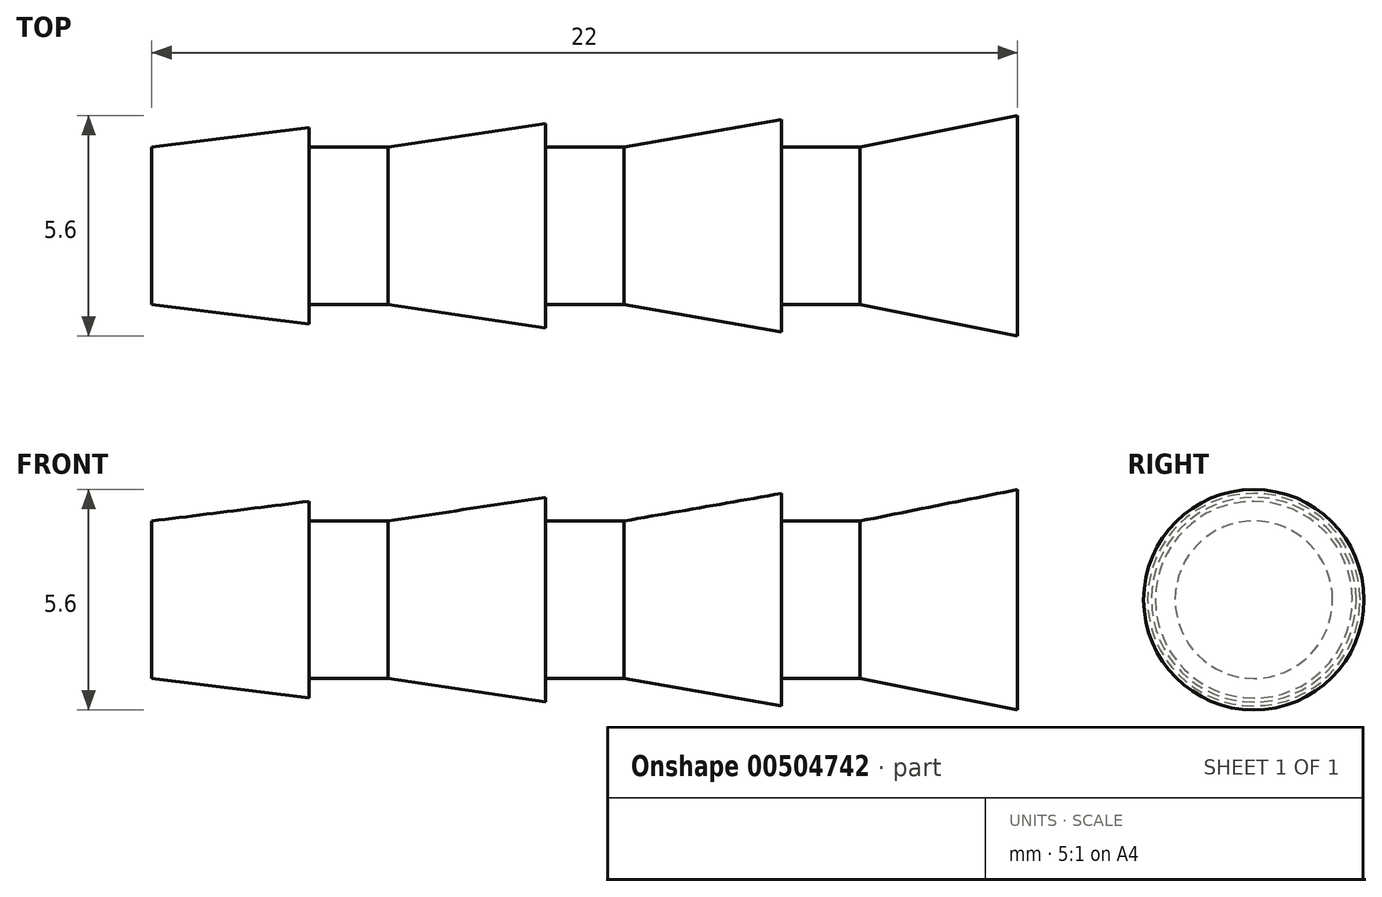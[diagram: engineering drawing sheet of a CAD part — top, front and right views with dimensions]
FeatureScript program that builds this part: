
annotation { "Feature Type Name" : "Feature", "Feature Type Description" : "" }
export const myFeature = defineFeature(function(context is Context, id is Id, definition is map)
    precondition{}
    {
        {
            var Q0;
            Q0=qCreatedBy(makeId("Front.planeOp"),FACE);
            var sketch = newSketch(context, id + "F0", { "sketchPlane" : qUnion([Q0])});
            skLineSegment(sketch, "E0", {"start": v(-13.38, 0) * mm, "end": v(33.35, 0) * mm, "construction": true});
            skLineSegment(sketch, "E1", {"start": v(-10.78, 0) * mm, "end": v(-10.78, 2) * mm});
            skLineSegment(sketch, "E2", {"start": v(-10.78, 2) * mm, "end": v(-6.78, 2.5) * mm});
            skLineSegment(sketch, "E3", {"start": v(-6.78, 2.5) * mm, "end": v(-6.78, 2) * mm});
            skLineSegment(sketch, "E4", {"start": v(-6.78, 2) * mm, "end": v(-4.78, 2) * mm});
            skLineSegment(sketch, "E5", {"start": v(-4.78, 2) * mm, "end": v(-0.78, 2.6) * mm});
            skLineSegment(sketch, "E6", {"start": v(-0.78, 2.6) * mm, "end": v(-0.78, 2) * mm});
            skLineSegment(sketch, "E7", {"start": v(-0.78, 2) * mm, "end": v(1.22, 2) * mm});
            skLineSegment(sketch, "E8", {"start": v(1.22, 2) * mm, "end": v(5.22, 2.7) * mm});
            skLineSegment(sketch, "E9", {"start": v(5.22, 2.7) * mm, "end": v(5.22, 2) * mm});
            skLineSegment(sketch, "E10", {"start": v(5.22, 2) * mm, "end": v(7.22, 2) * mm});
            skLineSegment(sketch, "E11", {"start": v(7.22, 2) * mm, "end": v(11.22, 2.8) * mm});
            skLineSegment(sketch, "E12", {"start": v(11.22, 2.8) * mm, "end": v(11.22, 0) * mm});
            skLineSegment(sketch, "E13", {"start": v(11.22, 0) * mm, "end": v(-10.78, 0) * mm});
            skSolve(sketch);
        }
        {
            var Q0;
            Q0 = qSketchRegion(id + "F0", true);
            var Q1;
            Q1=sQuery(id+"F0.wireOp",EDGE,"E0");
            revolve(context, id + "F1", {"entities" : qUnion([Q0]), "axis" : qUnion([Q1]), "revolveType" : RevolveType.FULL});
        }
    });
